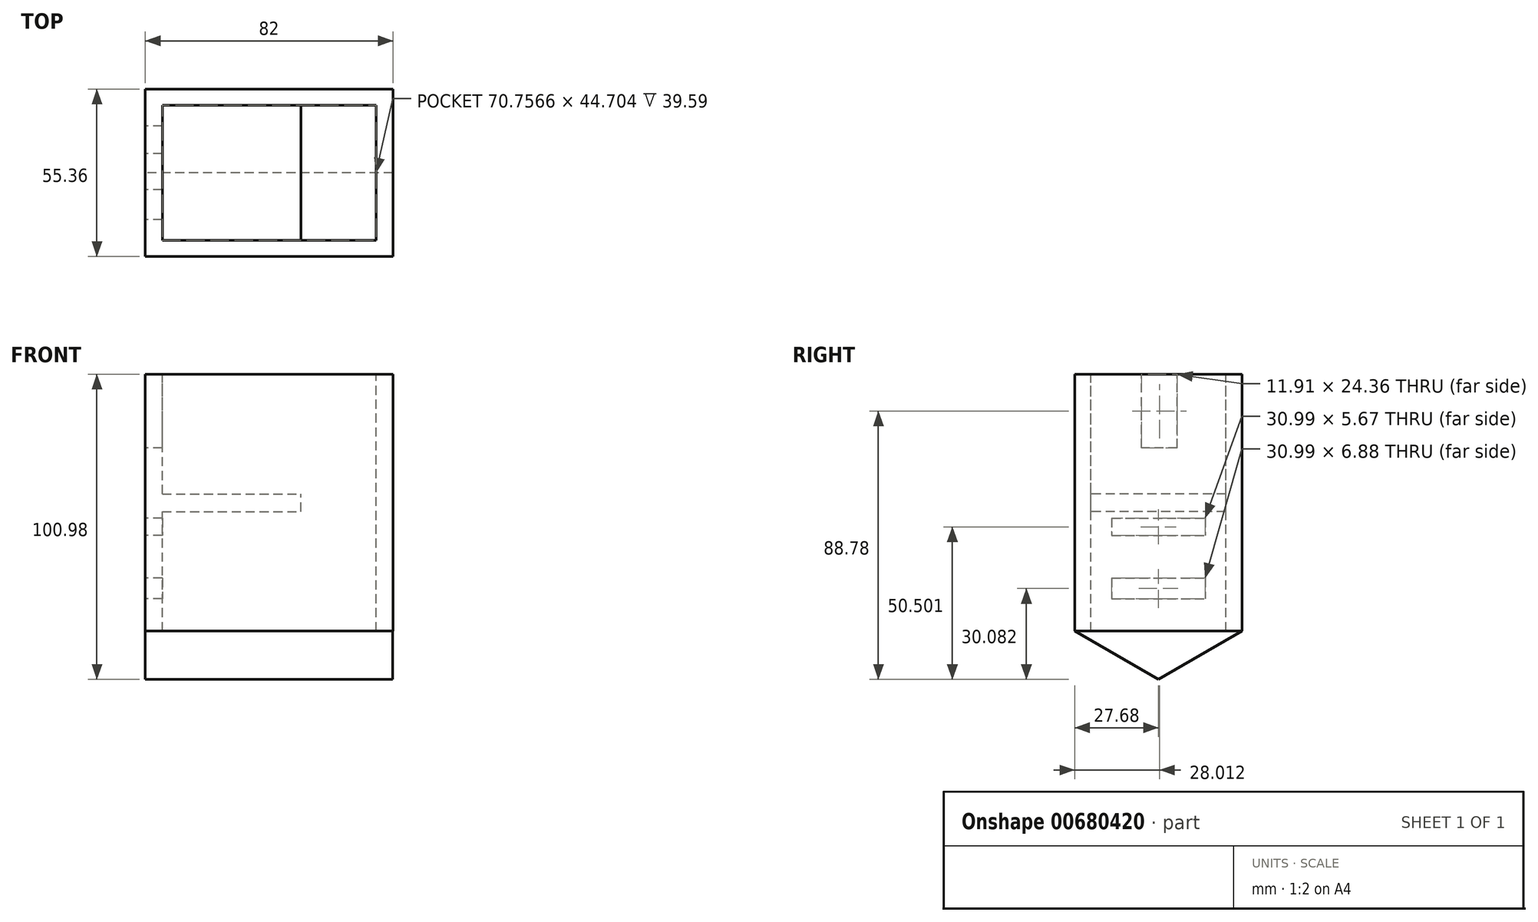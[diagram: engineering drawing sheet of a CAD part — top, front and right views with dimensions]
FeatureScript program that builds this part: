
annotation { "Feature Type Name" : "Feature", "Feature Type Description" : "" }
export const myFeature = defineFeature(function(context is Context, id is Id, definition is map)
    precondition{}
    {
        {
            var Q0;
            Q0=qCreatedBy(makeId("Top.planeOp"),FACE);
            var sketch = newSketch(context, id + "F0", { "sketchPlane" : qUnion([Q0])});
            skLineSegment(sketch, "E0.bottom", {"start": v(-41, 27.68) * mm, "end": v(41, 27.68) * mm});
            skLineSegment(sketch, "E0.top", {"start": v(-41, -27.68) * mm, "end": v(41, -27.68) * mm});
            skLineSegment(sketch, "E0.left", {"start": v(-41, 27.68) * mm, "end": v(-41, -27.68) * mm});
            skLineSegment(sketch, "E0.right", {"start": v(41, 27.68) * mm, "end": v(41, -27.68) * mm});
            skPoint(sketch, "E0.middle", {"position": v(0, 0) * mm});
            skSolve(sketch);
        }
        {
            var Q0;
            Q0 = qSketchRegion(id + "F0", true);
            extrude(context, id + "F1", {"entities" : qUnion([Q0]), "depth" : 85 * mm, "offsetDistance" : 25 * mm});
        }
        {
            var Q0;
            Q0=makeQuery(id+"F1.opExtrude","SWEPT_FACE",FACE,{"disambiguationData":[OSD([sQuery(id+"F0.wireOp",EDGE,"E0.left")])]});
            var sketch = newSketch(context, id + "F2", { "sketchPlane" : qUnion([Q0])});
            skLineSegment(sketch, "E1", {"start": v(-27.68, 0) * mm, "end": v(0, -15.98) * mm});
            skPoint(sketch, "E1.endSnap0", {"position": v(0, 85) * mm});
            skLineSegment(sketch, "E2", {"start": v(0, -15.98) * mm, "end": v(27.68, 0) * mm});
            skSolve(sketch);
        }
        {
            var Q0;
            Q0=makeQuery(id+"F2.imprint","IMPRINT",FACE,{"disambiguationData":[TD([[makeQuery(id+"F2.imprint","IMPRINT",EDGE,{"derivedFrom":sQuery(id+"F2.wireOp",EDGE,"E1")}),1.0]])]});
            extrude(context, id + "F3", {"entities" : qUnion([Q0]), "operationType" : NewBodyOperationType.ADD, "oppositeDirection" : true, "depth" : 81.9 * mm, "offsetDistance" : 25 * mm});
        }
        {
            var Q0;
            Q0=makeQuery(id+"F1.opExtrude","CAP_FACE",FACE,{"disambiguationData":[OSD([sQuery(id+"F0.wireOp",EDGE,"E0.bottom"),sQuery(id+"F0.wireOp",EDGE,"E0.top"),sQuery(id+"F0.wireOp",EDGE,"E0.left"),sQuery(id+"F0.wireOp",EDGE,"E0.right")])],"isStart":false});
            var sketch = newSketch(context, id + "F4", { "sketchPlane" : qUnion([Q0])});
            skLineSegment(sketch, "E3.bottom", {"start": v(-35.38, 22.35) * mm, "end": v(35.38, 22.35) * mm});
            skLineSegment(sketch, "E3.top", {"start": v(-35.38, -22.35) * mm, "end": v(35.38, -22.35) * mm});
            skLineSegment(sketch, "E3.left", {"start": v(-35.38, 22.35) * mm, "end": v(-35.38, -22.35) * mm});
            skLineSegment(sketch, "E3.right", {"start": v(35.38, 22.35) * mm, "end": v(35.38, -22.35) * mm});
            skPoint(sketch, "E3.middle", {"position": v(0, 0) * mm});
            skSolve(sketch);
        }
        {
            var Q0;
            Q0=makeQuery(id+"F4.imprint","IMPRINT",FACE,{"disambiguationData":[TD([[makeQuery(id+"F4.imprint","IMPRINT",EDGE,{"derivedFrom":sQuery(id+"F4.wireOp",EDGE,"E3.bottom")}),-1.0]])]});
            extrude(context, id + "F5", {"entities" : qUnion([Q0]), "operationType" : NewBodyOperationType.REMOVE, "oppositeDirection" : true, "depth" : 85 * mm, "offsetDistance" : 25 * mm});
        }
        {
            var Q0;
            {var subQ0=sQuery(id+"F0.wireOp",EDGE,"E0.left");Q0=makeQuery(id+"F2.imprint","IMPRINT",FACE,{"disambiguationData":[TD([[makeQuery(id+"F2.imprint","IMPRINT",EDGE,{"derivedFrom":makeQuery(id+"F1.opExtrude","CAP_EDGE",EDGE,{"disambiguationData":[OSD([subQ0])],"isStart":true})}),1.0]])]});}
            var sketch = newSketch(context, id + "F6", { "sketchPlane" : qUnion([Q0])});
            skLineSegment(sketch, "E4.bottom", {"start": v(15.5, 17.54) * mm, "end": v(-15.5, 17.54) * mm});
            skLineSegment(sketch, "E4.top", {"start": v(15.5, 10.66) * mm, "end": v(-15.5, 10.66) * mm});
            skLineSegment(sketch, "E4.left", {"start": v(15.5, 17.54) * mm, "end": v(15.5, 10.66) * mm});
            skLineSegment(sketch, "E4.right", {"start": v(-15.5, 17.54) * mm, "end": v(-15.5, 10.66) * mm});
            skPoint(sketch, "E4.middle", {"position": v(0, 14.1) * mm});
            skLineSegment(sketch, "E5.bottom", {"start": v(15.5, 37.36) * mm, "end": v(-15.5, 37.36) * mm});
            skLineSegment(sketch, "E5.top", {"start": v(15.5, 31.69) * mm, "end": v(-15.5, 31.69) * mm});
            skLineSegment(sketch, "E5.left", {"start": v(15.5, 37.36) * mm, "end": v(15.5, 31.69) * mm});
            skLineSegment(sketch, "E5.right", {"start": v(-15.5, 37.36) * mm, "end": v(-15.5, 31.69) * mm});
            skPoint(sketch, "E5.middle", {"position": v(0, 34.52) * mm});
            skLineSegment(sketch, "E6.bottom", {"start": v(-6.29, 60.62) * mm, "end": v(5.62, 60.62) * mm});
            skLineSegment(sketch, "E6.top", {"start": v(-6.29, 84.98) * mm, "end": v(5.62, 84.98) * mm});
            skLineSegment(sketch, "E6.left", {"start": v(-6.29, 60.62) * mm, "end": v(-6.29, 84.98) * mm});
            skLineSegment(sketch, "E6.right", {"start": v(5.62, 60.62) * mm, "end": v(5.62, 84.98) * mm});
            skSolve(sketch);
        }
        {
            var Q0;
            Q0=makeQuery(id+"F6.imprint","IMPRINT",FACE,{"disambiguationData":[TD([[makeQuery(id+"F6.imprint","IMPRINT",EDGE,{"derivedFrom":sQuery(id+"F6.wireOp",EDGE,"E4.bottom")}),1.0]])]});
            var Q1;
            Q1=makeQuery(id+"F6.imprint","IMPRINT",FACE,{"disambiguationData":[TD([[makeQuery(id+"F6.imprint","IMPRINT",EDGE,{"derivedFrom":sQuery(id+"F6.wireOp",EDGE,"E5.bottom")}),1.0]])]});
            var Q2;
            Q2=makeQuery(id+"F6.imprint","IMPRINT",FACE,{"disambiguationData":[TD([[makeQuery(id+"F6.imprint","IMPRINT",EDGE,{"derivedFrom":sQuery(id+"F6.wireOp",EDGE,"E6.bottom")}),1.0]])]});
            extrude(context, id + "F7", {"entities" : qUnion([Q0, Q1, Q2]), "operationType" : NewBodyOperationType.REMOVE, "oppositeDirection" : true, "depth" : 55 * mm, "offsetDistance" : 25 * mm});
        }
        {
            var Q0;
            Q0=makeQuery(id+"F1.opExtrude","SWEPT_FACE",FACE,{"disambiguationData":[OSD([sQuery(id+"F0.wireOp",EDGE,"E0.right")])]});
            var sketch = newSketch(context, id + "F8", { "sketchPlane" : qUnion([Q0])});
            skLineSegment(sketch, "E7.bottom", {"start": v(-27.68, 45.4) * mm, "end": v(27.68, 45.4) * mm});
            skLineSegment(sketch, "E7.top", {"start": v(-27.68, 39.6) * mm, "end": v(27.68, 39.6) * mm});
            skLineSegment(sketch, "E7.left", {"start": v(-27.68, 45.4) * mm, "end": v(-27.68, 39.6) * mm});
            skLineSegment(sketch, "E7.right", {"start": v(27.68, 45.4) * mm, "end": v(27.68, 39.6) * mm});
            skPoint(sketch, "E7.middle", {"position": v(0, 42.5) * mm});
            skPoint(sketch, "E7.middle.positionSnap0", {"position": v(-27.68, 42.5) * mm});
            skPoint(sketch, "E7.centerSnap0", {"position": v(-27.68, 42.5) * mm});
            skSolve(sketch);
        }
        {
            var Q0;
            Q0=makeQuery(id+"F8.imprint","IMPRINT",FACE,{"disambiguationData":[TD([[makeQuery(id+"F8.imprint","IMPRINT",EDGE,{"derivedFrom":sQuery(id+"F8.wireOp",EDGE,"E7.bottom")}),-1.0]])]});
            extrude(context, id + "F9", {"entities" : qUnion([Q0]), "operationType" : NewBodyOperationType.ADD, "oppositeDirection" : true, "depth" : 78.5 * mm, "offsetDistance" : 25 * mm, "hasSecondDirection" : true, "secondDirectionOppositeDirection" : true, "secondDirectionDepth" : 30.5 * mm});
        }
    });
